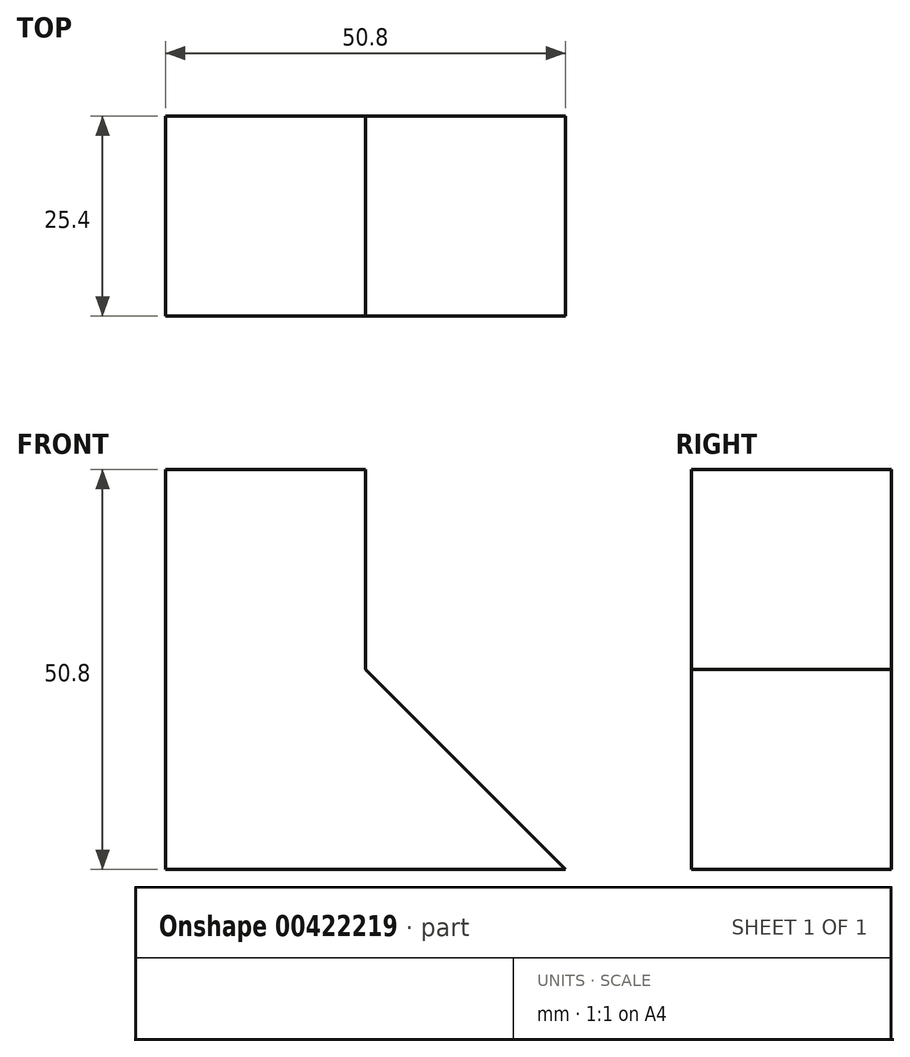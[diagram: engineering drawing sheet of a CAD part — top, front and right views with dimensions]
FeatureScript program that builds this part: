
annotation { "Feature Type Name" : "Feature", "Feature Type Description" : "" }
export const myFeature = defineFeature(function(context is Context, id is Id, definition is map)
    precondition{}
    {
        {
            var Q0;
            Q0=qCreatedBy(makeId("Front.planeOp"),FACE);
            var sketch = newSketch(context, id + "F0", { "sketchPlane" : qUnion([Q0])});
            skLineSegment(sketch, "E0", {"start": v(0, 0) * mm, "end": v(-50.8, 0) * mm});
            skLineSegment(sketch, "E1", {"start": v(-50.8, 50.8) * mm, "end": v(-50.8, 0) * mm});
            skLineSegment(sketch, "E2", {"start": v(-50.8, 50.8) * mm, "end": v(-25.4, 50.8) * mm});
            skLineSegment(sketch, "E3", {"start": v(-25.4, 25.4) * mm, "end": v(-25.4, 50.8) * mm});
            skLineSegment(sketch, "E4", {"start": v(-25.4, 25.4) * mm, "end": v(0, 0) * mm});
            skSolve(sketch);
        }
        {
            var Q0;
            Q0 = qSketchRegion(id + "F0", true);
            extrude(context, id + "F1", {"entities" : qUnion([Q0]), "depth" : 25.4 * mm});
        }
    });
